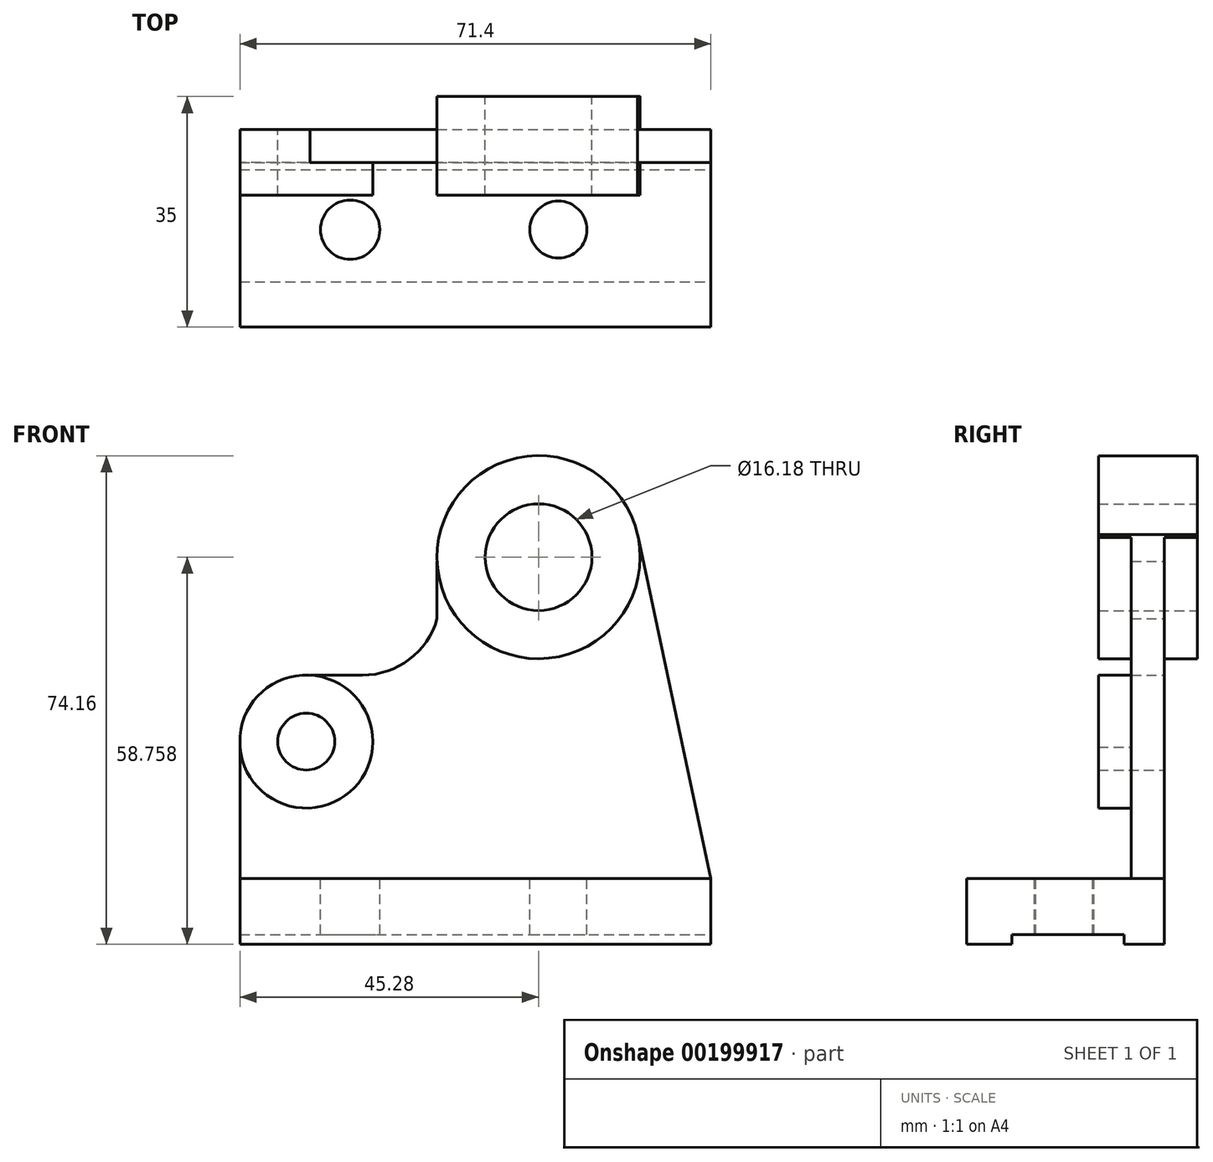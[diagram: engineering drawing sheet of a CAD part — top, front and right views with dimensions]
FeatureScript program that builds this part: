
annotation { "Feature Type Name" : "Feature", "Feature Type Description" : "" }
export const myFeature = defineFeature(function(context is Context, id is Id, definition is map)
    precondition{}
    {
        {
            var Q0;
            Q0=qCreatedBy(makeId("Front.planeOp"),FACE);
            var sketch = newSketch(context, id + "F0", { "sketchPlane" : qUnion([Q0])});
            skLineSegment(sketch, "E0", {"start": v(-35.26, 0) * mm, "end": v(36.14, 0) * mm});
            skLineSegment(sketch, "E1", {"start": v(36.14, 0) * mm, "end": v(36.14, 10.02) * mm});
            skLineSegment(sketch, "E2", {"start": v(36.14, 10.02) * mm, "end": v(-35.26, 10.02) * mm});
            skLineSegment(sketch, "E3", {"start": v(-35.26, 10.02) * mm, "end": v(-35.26, 0) * mm});
            skLineSegment(sketch, "E4", {"start": v(36.14, 10.02) * mm, "end": v(25.04, 62.16) * mm});
            skCircle(sketch, "E5", {"center": v(10.02, 58.76) * mm, "radius": 15.4 * mm});
            skPoint(sketch, "E5.second.point", {"position": v(-5.37, 58.13) * mm});
            skPoint(sketch, "E5.third.point", {"position": v(16.82, 44.94) * mm});
            skLineSegment(sketch, "E6", {"start": v(-35.26, 10.02) * mm, "end": v(-35.26, 31.6) * mm});
            skCircle(sketch, "E7", {"center": v(-25.2, 30.77) * mm, "radius": 10.1 * mm});
            skPoint(sketch, "E7.second.point", {"position": v(-15.14, 31.6) * mm});
            skPoint(sketch, "E7.third.point", {"position": v(-21.2, 21.51) * mm});
            skLineSegment(sketch, "E8", {"start": v(-24.62, 40.85) * mm, "end": v(-16.7, 40.85) * mm});
            skLineSegment(sketch, "E9", {"start": v(-5.37, 58.13) * mm, "end": v(-5.37, 49.44) * mm});
            skArc(sketch, "E10", {"start": v(-16.7, 40.85) * mm, "mid": v(-9.59, 43.24) * mm, "end": v(-5.37, 49.44) * mm});
            skCircle(sketch, "E11", {"center": v(-25.2, 30.77) * mm, "radius": 4.32 * mm});
            skCircle(sketch, "E12", {"center": v(10.02, 58.76) * mm, "radius": 8.1 * mm});
            skSolve(sketch);
        }
        {
            var Q0;
            Q0=makeQuery(id+"F0.imprint","IMPRINT",FACE,{"disambiguationData":[TD([[makeQuery(id+"F0.imprint","IMPRINT",EDGE,{"derivedFrom":sQuery(id+"F0.wireOp",EDGE,"E0")}),1.0]])]});
            extrude(context, id + "F1", {"entities" : qUnion([Q0]), "depth" : 30 * mm});
        }
        {
            var Q0;
            {var subQ1=sQuery(id+"F0.wireOp",EDGE,"E2");Q0=makeQuery(id+"F0.imprint","IMPRINT",FACE,{"disambiguationData":[TD([[makeQuery(id+"F0.imprint","IMPRINT",EDGE,{"derivedFrom":subQ1}),-1.0]])]});}
            var Q1;
            Q1=makeQuery(id+"F0.imprint","IMPRINT",FACE,{"disambiguationData":[TD([[makeQuery(id+"F0.imprint","IMPRINT",EDGE,{"derivedFrom":sQuery(id+"F0.wireOp",EDGE,"E12")}),-1.0]])]});
            extrude(context, id + "F2", {"entities" : qUnion([Q0, Q1]), "operationType" : NewBodyOperationType.ADD, "depth" : 5 * mm});
        }
        {
            var Q0;
            Q0=makeQuery(id+"F0.imprint","IMPRINT",FACE,{"disambiguationData":[TD([[makeQuery(id+"F0.imprint","IMPRINT",EDGE,{"derivedFrom":sQuery(id+"F0.wireOp",EDGE,"E12")}),-1.0]])]});
            extrude(context, id + "F3", {"entities" : qUnion([Q0]), "operationType" : NewBodyOperationType.ADD, "depth" : 10 * mm});
        }
        {
            var Q0;
            Q0=makeQuery(id+"F0.imprint","IMPRINT",FACE,{"disambiguationData":[TD([[makeQuery(id+"F0.imprint","IMPRINT",EDGE,{"derivedFrom":sQuery(id+"F0.wireOp",EDGE,"E12")}),-1.0]])]});
            extrude(context, id + "F4", {"entities" : qUnion([Q0]), "operationType" : NewBodyOperationType.ADD, "oppositeDirection" : true, "depth" : 5 * mm});
        }
        {
            var Q0;
            Q0=makeQuery(id+"F0.imprint","IMPRINT",FACE,{"disambiguationData":[TD([[makeQuery(id+"F0.imprint","IMPRINT",EDGE,{"derivedFrom":sQuery(id+"F0.wireOp",EDGE,"E11")}),-1.0]])]});
            extrude(context, id + "F5", {"entities" : qUnion([Q0]), "operationType" : NewBodyOperationType.ADD, "depth" : 10 * mm});
        }
        {
            var Q0;
            Q0=makeQuery(id+"F1.opExtrude","SWEPT_FACE",FACE,{"disambiguationData":[OSD([sQuery(id+"F0.wireOp",EDGE,"E2")])]});
            var sketch = newSketch(context, id + "F6", { "sketchPlane" : qUnion([Q0])});
            skCircle(sketch, "E13", {"center": v(-18.54, -15.2) * mm, "radius": 4.5 * mm});
            skCircle(sketch, "E14", {"center": v(13.03, -15.2) * mm, "radius": 4.33 * mm});
            skSolve(sketch);
        }
        {
            var Q0;
            Q0=makeQuery(id+"F6.imprint","IMPRINT",FACE,{"disambiguationData":[TD([[makeQuery(id+"F6.imprint","IMPRINT",EDGE,{"derivedFrom":sQuery(id+"F6.wireOp",EDGE,"E13")}),1.0]])]});
            var Q1;
            Q1=makeQuery(id+"F6.imprint","IMPRINT",FACE,{"disambiguationData":[TD([[makeQuery(id+"F6.imprint","IMPRINT",EDGE,{"derivedFrom":sQuery(id+"F6.wireOp",EDGE,"E14")}),1.0]])]});
            extrude(context, id + "F7", {"entities" : qUnion([Q0, Q1]), "operationType" : NewBodyOperationType.REMOVE, "oppositeDirection" : true, "depth" : 10 * mm});
        }
        {
            var Q0;
            Q0=makeQuery(id+"F1.opExtrude","SWEPT_FACE",FACE,{"disambiguationData":[OSD([sQuery(id+"F0.wireOp",EDGE,"E1")])]});
            var sketch = newSketch(context, id + "F8", { "sketchPlane" : qUnion([Q0])});
            skLineSegment(sketch, "E15", {"start": v(-23.12, 0) * mm, "end": v(-23.12, 1.5) * mm});
            skLineSegment(sketch, "E16", {"start": v(-23.12, 1.5) * mm, "end": v(-6.12, 1.5) * mm});
            skLineSegment(sketch, "E17", {"start": v(-6.12, 1.5) * mm, "end": v(-6.12, 0) * mm});
            skSolve(sketch);
        }
        {
            var Q0;
            {var subQ0=sQuery(id+"F8.wireOp",EDGE,"E15");Q0=makeQuery(id+"F8.imprint","IMPRINT",FACE,{"disambiguationData":[TD([[makeQuery(id+"F8.imprint","IMPRINT",EDGE,{"derivedFrom":subQ0}),-1.0]])]});}
            extrude(context, id + "F9", {"entities" : qUnion([Q0]), "operationType" : NewBodyOperationType.REMOVE, "oppositeDirection" : true, "depth" : 75 * mm});
        }
    });
